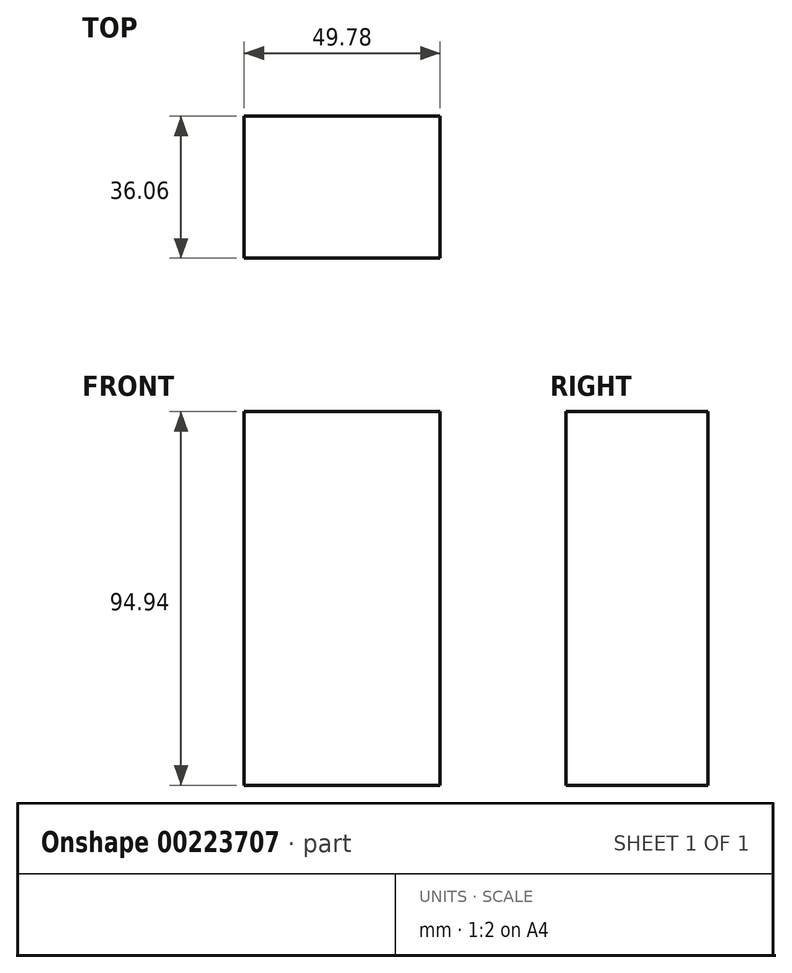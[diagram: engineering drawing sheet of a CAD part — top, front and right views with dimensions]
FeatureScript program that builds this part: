
annotation { "Feature Type Name" : "Feature", "Feature Type Description" : "" }
export const myFeature = defineFeature(function(context is Context, id is Id, definition is map)
    precondition{}
    {
        {
            var Q0;
            Q0=qCreatedBy(makeId("Front.planeOp"),FACE);
            var sketch = newSketch(context, id + "F0", { "sketchPlane" : qUnion([Q0])});
            skLineSegment(sketch, "E0.bottom", {"start": v(-24.9, 47.47) * mm, "end": v(24.9, 47.47) * mm});
            skLineSegment(sketch, "E0.top", {"start": v(-24.9, -47.47) * mm, "end": v(24.9, -47.47) * mm});
            skLineSegment(sketch, "E0.left", {"start": v(-24.9, 47.47) * mm, "end": v(-24.9, -47.47) * mm});
            skLineSegment(sketch, "E0.right", {"start": v(24.9, 47.47) * mm, "end": v(24.9, -47.47) * mm});
            skPoint(sketch, "E0.middle", {"position": v(0, 0) * mm});
            skSolve(sketch);
        }
        {
            var Q0;
            Q0 = qSketchRegion(id + "F0", true);
            extrude(context, id + "F1", {"entities" : qUnion([Q0]), "endBound" : BoundingType.SYMMETRIC, "depth" : 36.07 * mm});
        }
    });
